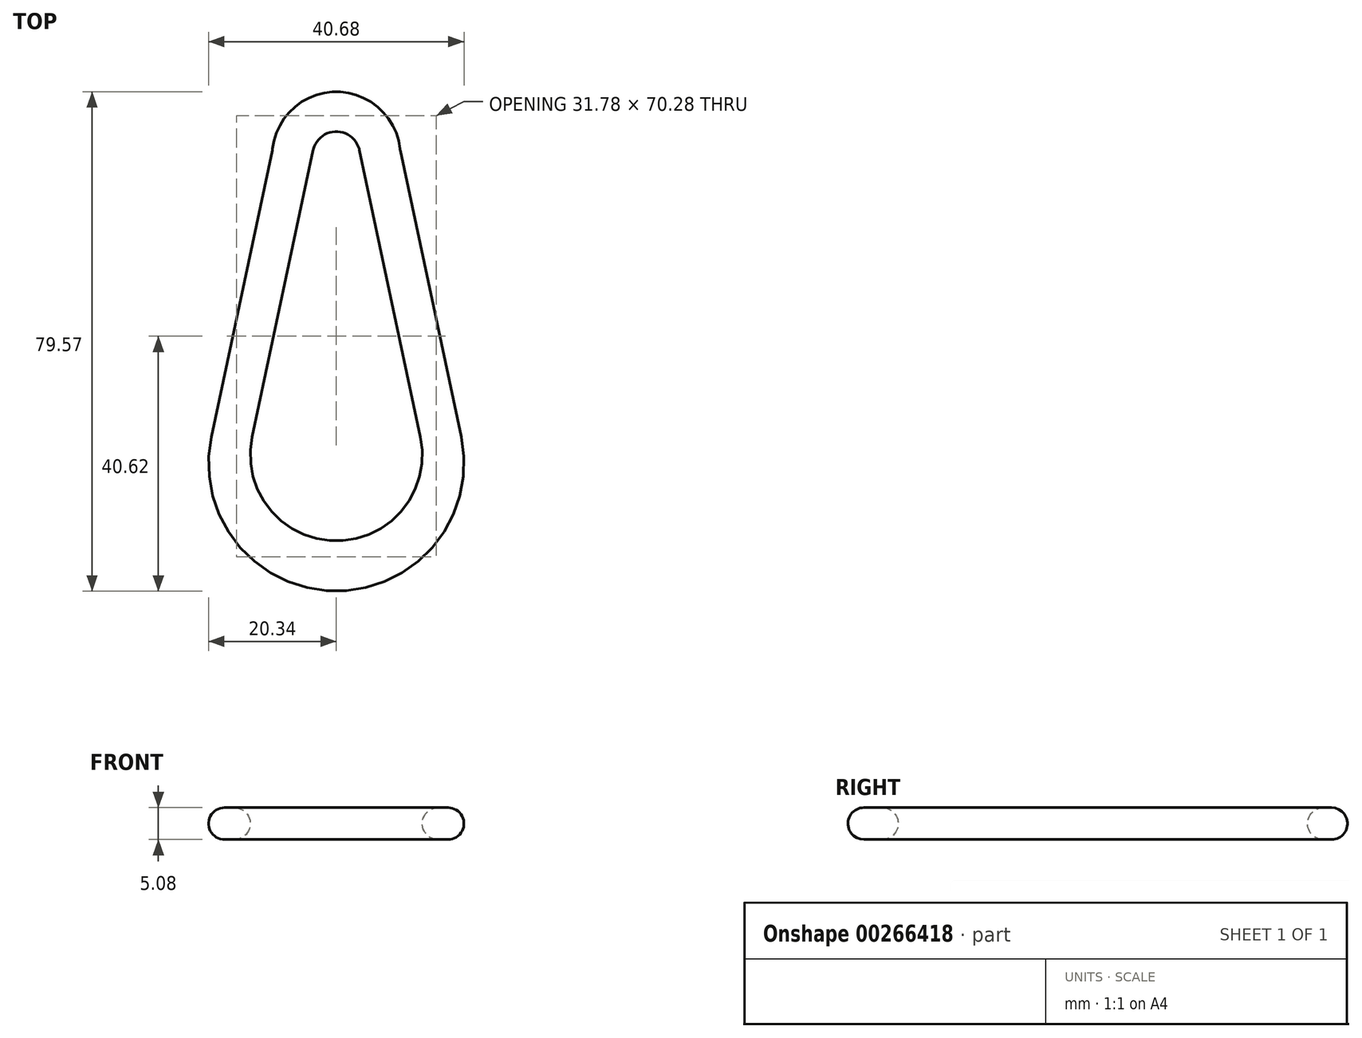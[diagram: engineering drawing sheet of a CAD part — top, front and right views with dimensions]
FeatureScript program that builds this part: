
annotation { "Feature Type Name" : "Feature", "Feature Type Description" : "" }
export const myFeature = defineFeature(function(context is Context, id is Id, definition is map)
    precondition{}
    {
        {
            var Q0;
            Q0=qCreatedBy(makeId("Top.planeOp"),FACE);
            var sketch = newSketch(context, id + "F0", { "sketchPlane" : qUnion([Q0])});
            skLineSegment(sketch, "E0", {"start": v(0, 37.9) * mm, "end": v(0, -30.01) * mm, "construction": true});
            skLineSegment(sketch, "E1", {"start": v(10.16, 24.42) * mm, "end": v(19.9, -21.38) * mm});
            skLineSegment(sketch, "E2", {"start": v(-10.16, 24.42) * mm, "end": v(-19.9, -21.38) * mm});
            skArc(sketch, "E3", {"start": v(-19.9, -21.38) * mm, "mid": v(0, -45.95) * mm, "end": v(19.9, -21.38) * mm});
            skLineSegment(sketch, "E4", {"start": v(3.67, 24.42) * mm, "end": v(13.4, -21.38) * mm});
            skLineSegment(sketch, "E5", {"start": v(-3.67, 24.42) * mm, "end": v(-13.4, -21.38) * mm});
            skArc(sketch, "E6", {"start": v(-13.4, -21.38) * mm, "mid": v(0, -37.93) * mm, "end": v(13.4, -21.38) * mm});
            skArc(sketch, "E7", {"start": v(10.16, 24.42) * mm, "mid": v(0, 33.62) * mm, "end": v(-10.16, 24.42) * mm});
            skArc(sketch, "E8", {"start": v(3.67, 24.42) * mm, "mid": v(0, 27.27) * mm, "end": v(-3.67, 24.42) * mm});
            skSolve(sketch);
        }
        {
            var Q0;
            Q0 = qSketchRegion(id + "F0", true);
            extrude(context, id + "F1", {"entities" : qUnion([Q0]), "oppositeDirection" : true, "depth" : 2.54 * mm, "hasSecondDirection" : true, "secondDirectionOppositeDirection" : false, "secondDirectionDepth" : 2.54 * mm});
        }
        {
            var Q0;
            Q0=makeQuery(id+"F1.opExtrude","SWEPT_FACE",FACE,{"disambiguationData":[OSD([sQuery(id+"F0.wireOp",EDGE,"E5")])]});
            var Q1;
            Q1=makeQuery(id+"F1.opExtrude","CAP_EDGE",EDGE,{"disambiguationData":[OSD([sQuery(id+"F0.wireOp",EDGE,"E3")])],"isStart":false});
            var Q2;
            Q2=makeQuery(id+"F1.opExtrude","SWEPT_FACE",FACE,{"disambiguationData":[OSD([sQuery(id+"F0.wireOp",EDGE,"E6")])]});
            var Q3;
            Q3=makeQuery(id+"F1.opExtrude","SWEPT_FACE",FACE,{"disambiguationData":[OSD([sQuery(id+"F0.wireOp",EDGE,"E1")])]});
            var Q4;
            Q4=makeQuery(id+"F1.opExtrude","CAP_FACE",FACE,{"disambiguationData":[OSD([sQuery(id+"F0.wireOp",EDGE,"E1"),sQuery(id+"F0.wireOp",EDGE,"E2"),sQuery(id+"F0.wireOp",EDGE,"E3"),sQuery(id+"F0.wireOp",EDGE,"E4"),sQuery(id+"F0.wireOp",EDGE,"E5"),sQuery(id+"F0.wireOp",EDGE,"E6"),sQuery(id+"F0.wireOp",EDGE,"E7"),sQuery(id+"F0.wireOp",EDGE,"E8")])],"isStart":true});
            var Q5;
            Q5=makeQuery(id+"F1.opExtrude","SWEPT_FACE",FACE,{"disambiguationData":[OSD([sQuery(id+"F0.wireOp",EDGE,"E7")])]});
            var Q6;
            Q6=makeQuery(id+"F1.opExtrude","CAP_EDGE",EDGE,{"disambiguationData":[OSD([sQuery(id+"F0.wireOp",EDGE,"E2")])],"isStart":true});
            var Q7;
            Q7=makeQuery(id+"F1.opExtrude","CAP_FACE",FACE,{"disambiguationData":[OSD([sQuery(id+"F0.wireOp",EDGE,"E1"),sQuery(id+"F0.wireOp",EDGE,"E2"),sQuery(id+"F0.wireOp",EDGE,"E3"),sQuery(id+"F0.wireOp",EDGE,"E4"),sQuery(id+"F0.wireOp",EDGE,"E5"),sQuery(id+"F0.wireOp",EDGE,"E6"),sQuery(id+"F0.wireOp",EDGE,"E7"),sQuery(id+"F0.wireOp",EDGE,"E8")])],"isStart":false});
            var Q8;
            Q8=makeQuery(id+"F1.opExtrude","SWEPT_FACE",FACE,{"disambiguationData":[OSD([sQuery(id+"F0.wireOp",EDGE,"E2")])]});
            var Q9;
            Q9=makeQuery(id+"F1.opExtrude","CAP_EDGE",EDGE,{"disambiguationData":[OSD([sQuery(id+"F0.wireOp",EDGE,"E6")])],"isStart":true});
            var Q10;
            Q10=makeQuery(id+"F1.opExtrude","CAP_EDGE",EDGE,{"disambiguationData":[OSD([sQuery(id+"F0.wireOp",EDGE,"E8")])],"isStart":true});
            var Q11;
            Q11=makeQuery(id+"F1.opExtrude","SWEPT_FACE",FACE,{"disambiguationData":[OSD([sQuery(id+"F0.wireOp",EDGE,"E8")])]});
            var Q12;
            Q12=makeQuery(id+"F1.opExtrude","CAP_EDGE",EDGE,{"disambiguationData":[OSD([sQuery(id+"F0.wireOp",EDGE,"E1")])],"isStart":false});
            var Q13;
            Q13=makeQuery(id+"F1.opExtrude","SWEPT_FACE",FACE,{"disambiguationData":[OSD([sQuery(id+"F0.wireOp",EDGE,"E3")])]});
            var Q14;
            Q14=makeQuery(id+"F1.opExtrude","CAP_EDGE",EDGE,{"disambiguationData":[OSD([sQuery(id+"F0.wireOp",EDGE,"E5")])],"isStart":true});
            var Q15;
            Q15=makeQuery(id+"F1.opExtrude","CAP_EDGE",EDGE,{"disambiguationData":[OSD([sQuery(id+"F0.wireOp",EDGE,"E7")])],"isStart":false});
            var Q16;
            Q16=makeQuery(id+"F1.opExtrude","CAP_EDGE",EDGE,{"disambiguationData":[OSD([sQuery(id+"F0.wireOp",EDGE,"E7")])],"isStart":true});
            var Q17;
            Q17=makeQuery(id+"F1.opExtrude","CAP_EDGE",EDGE,{"disambiguationData":[OSD([sQuery(id+"F0.wireOp",EDGE,"E3")])],"isStart":true});
            var Q18;
            Q18=makeQuery(id+"F1.opExtrude","CAP_EDGE",EDGE,{"disambiguationData":[OSD([sQuery(id+"F0.wireOp",EDGE,"E5")])],"isStart":false});
            var Q19;
            Q19=makeQuery(id+"F1.opExtrude","CAP_EDGE",EDGE,{"disambiguationData":[OSD([sQuery(id+"F0.wireOp",EDGE,"E6")])],"isStart":false});
            var Q20;
            Q20=makeQuery(id+"F1.opExtrude","CAP_EDGE",EDGE,{"disambiguationData":[OSD([sQuery(id+"F0.wireOp",EDGE,"E8")])],"isStart":false});
            var Q21;
            Q21=makeQuery(id+"F1.opExtrude","SWEPT_FACE",FACE,{"disambiguationData":[OSD([sQuery(id+"F0.wireOp",EDGE,"E4")])]});
            var Q22;
            Q22=makeQuery(id+"F1.opExtrude","SWEPT_EDGE",EDGE,{"disambiguationData":[OSD([sQuery(id+"F0.wireOp",EDGE,"E5"),sQuery(id+"F0.wireOp",EDGE,"E8")])]});
            var Q23;
            Q23=makeQuery(id+"F1.opExtrude","CAP_EDGE",EDGE,{"disambiguationData":[OSD([sQuery(id+"F0.wireOp",EDGE,"E1")])],"isStart":true});
            var Q24;
            Q24=makeQuery(id+"F1.opExtrude","SWEPT_EDGE",EDGE,{"disambiguationData":[OSD([sQuery(id+"F0.wireOp",EDGE,"E1"),sQuery(id+"F0.wireOp",EDGE,"E7")])]});
            var Q25;
            Q25=makeQuery(id+"F1.opExtrude","CAP_EDGE",EDGE,{"disambiguationData":[OSD([sQuery(id+"F0.wireOp",EDGE,"E4")])],"isStart":false});
            var Q26;
            Q26=makeQuery(id+"F1.opExtrude","SWEPT_EDGE",EDGE,{"disambiguationData":[OSD([sQuery(id+"F0.wireOp",EDGE,"E1"),sQuery(id+"F0.wireOp",EDGE,"E3")])]});
            var Q27;
            Q27=makeQuery(id+"F1.opExtrude","SWEPT_EDGE",EDGE,{"disambiguationData":[OSD([sQuery(id+"F0.wireOp",EDGE,"E2"),sQuery(id+"F0.wireOp",EDGE,"E3")])]});
            var Q28;
            Q28=makeQuery(id+"F1.opExtrude","SWEPT_EDGE",EDGE,{"disambiguationData":[OSD([sQuery(id+"F0.wireOp",EDGE,"E5"),sQuery(id+"F0.wireOp",EDGE,"E6")])]});
            var Q29;
            Q29=makeQuery(id+"F1.opExtrude","SWEPT_EDGE",EDGE,{"disambiguationData":[OSD([sQuery(id+"F0.wireOp",EDGE,"E4"),sQuery(id+"F0.wireOp",EDGE,"E8")])]});
            var Q30;
            Q30=makeQuery(id+"F1.opExtrude","SWEPT_EDGE",EDGE,{"disambiguationData":[OSD([sQuery(id+"F0.wireOp",EDGE,"E4"),sQuery(id+"F0.wireOp",EDGE,"E6")])]});
            var Q31;
            Q31=makeQuery(id+"F1.opExtrude","SWEPT_EDGE",EDGE,{"disambiguationData":[OSD([sQuery(id+"F0.wireOp",EDGE,"E2"),sQuery(id+"F0.wireOp",EDGE,"E7")])]});
            var Q32;
            Q32=makeQuery(id+"F1.opExtrude","CAP_EDGE",EDGE,{"disambiguationData":[OSD([sQuery(id+"F0.wireOp",EDGE,"E2")])],"isStart":false});
            var Q33;
            Q33=makeQuery(id+"F1.opExtrude","CAP_EDGE",EDGE,{"disambiguationData":[OSD([sQuery(id+"F0.wireOp",EDGE,"E4")])],"isStart":true});
            fillet(context, id + "F2", {"entities" : qUnion([Q0, Q1, Q2, Q3, Q4, Q5, Q6, Q7, Q8, Q9, Q10, Q11, Q12, Q13, Q14, Q15, Q16, Q17, Q18, Q19, Q20, Q21, Q22, Q23, Q24, Q25, Q26, Q27, Q28, Q29, Q30, Q31, Q32, Q33]), "radius" : 2.54 * mm, "tangentPropagation" : true, "allowEdgeOverflow" : false});
        }
    });
